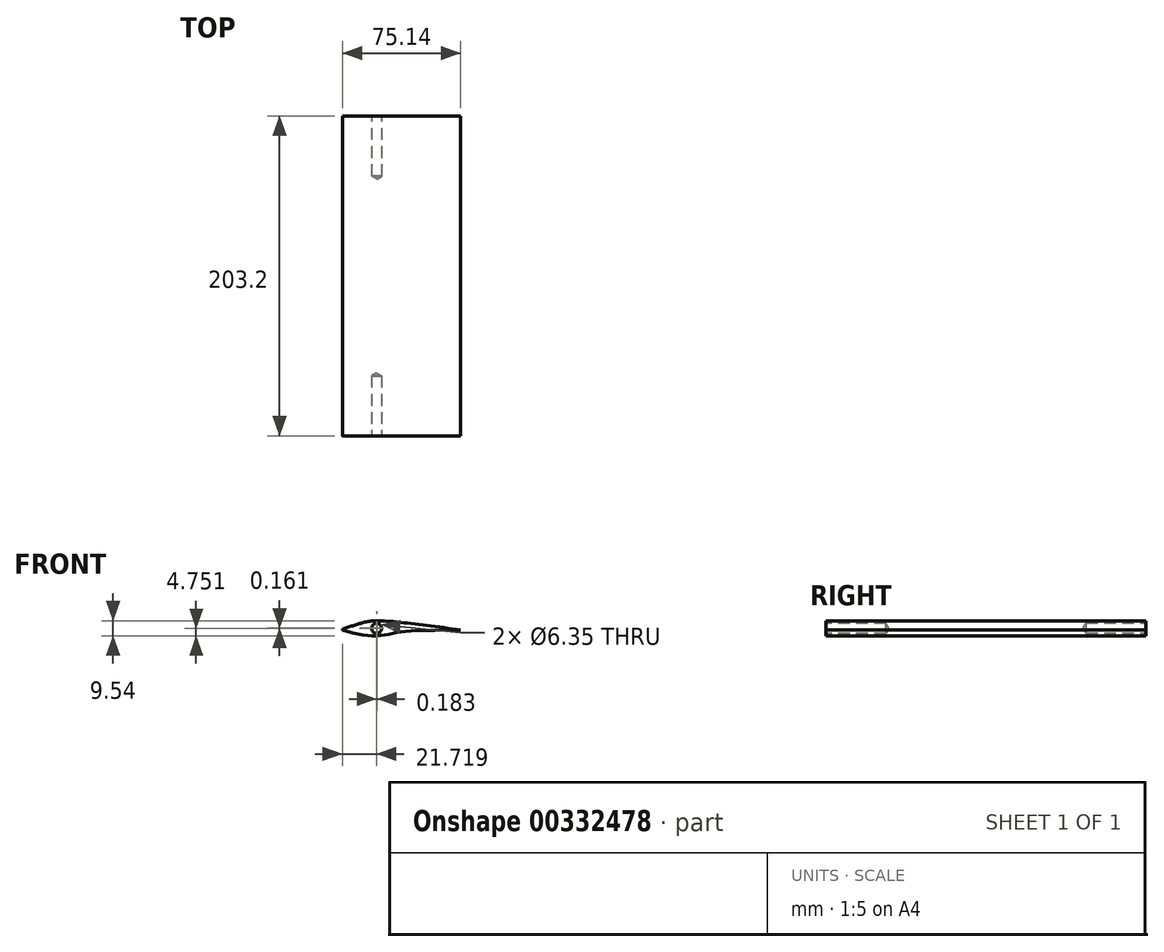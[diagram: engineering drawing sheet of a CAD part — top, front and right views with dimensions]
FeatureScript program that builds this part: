
annotation { "Feature Type Name" : "Feature", "Feature Type Description" : "" }
export const myFeature = defineFeature(function(context is Context, id is Id, definition is map)
    precondition{}
    {
        {
            var Q0;
            Q0=qCreatedBy(makeId("Front.planeOp"),FACE);
            var sketch = newSketch(context, id + "F0", { "sketchPlane" : qUnion([Q0])});
            skLineSegment(sketch, "E0", {"start": v(-15.24, -3.9) * mm, "end": v(-15.24, -3.9) * mm});
            skFitSpline(sketch, "E1", {"points": [v(-38.1, 0) * mm, v(-27.43, 3.47) * mm, v(-15.5, 5.63) * mm, v(38.1, 0) * mm], "startDerivative": vector(46.4, 16.4) * mm, "endDerivative": vector(122.48, -13.67) * mm});
            skFitSpline(sketch, "E2", {"points": [v(-38.1, 0) * mm, v(-15.24, -3.9) * mm, v(1.87, -1.13) * mm, v(38.1, 0) * mm], "startDerivative": vector(68.69, -19.73) * mm, "endDerivative": vector(99.76, 4.28) * mm});
            skPoint(sketch, "E3.endSnap0", {"position": v(-15.24, 3.44) * mm});
            skPoint(sketch, "E4.orphan", {"position": v(0, 0) * mm});
            skArc(sketch, "E5.trimOffspring", {"start": v(-15.2, 5.63) * mm, "mid": v(-15.22, 5.63) * mm, "end": v(-15.24, 5.63) * mm});
            skPoint(sketch, "E6.end.orphan", {"position": v(-15.22, 6.02) * mm});
            skPoint(sketch, "E7.trimOffspring.end.orphan", {"position": v(-15.24, -7.6) * mm});
            skSolve(sketch);
        }
        {
            var Q0;
            Q0 = qSketchRegion(id + "F0", true);
            extrude(context, id + "F1", {"entities" : qUnion([Q0]), "oppositeDirection" : true, "depth" : 203.2 * mm});
        }
        {
            var Q0;
            {var subQ0=sQuery(id+"F0.wireOp",EDGE,"E2");var subQ1=sQuery(id+"F0.wireOp",EDGE,"E1");Q0=makeQuery(id+"F1.opExtrude","SWEPT_EDGE",EDGE,{"disambiguationData":[OSD([subQ1,subQ0]),TDD([makeQuery(id+"F0.imprint","INTERSECT",VERTEX,{"disambiguationData":[OD(0.0)],"derivedFrom":[subQ1,subQ0]})])]});}
            fillet(context, id + "F2", {"entities" : qUnion([Q0]), "radius" : 0.46 * mm, "tangentPropagation" : true, "allowEdgeOverflow" : false});
        }
        {
            var Q0;
            Q0=makeQuery(id+"F1.opExtrude","CAP_FACE",FACE,{"disambiguationData":[OSD([sQuery(id+"F0.wireOp",EDGE,"E1"),sQuery(id+"F0.wireOp",EDGE,"E2")])],"isStart":false});
            var sketch = newSketch(context, id + "F3", { "sketchPlane" : qUnion([Q0])});
            skPoint(sketch, "E8", {"position": v(15.14, 1.01) * mm});
            skSolve(sketch);
        }
        {
            var Q0;
            Q0=sQuery(id+"F3.wireOp",VERTEX,"E8");
            var Q1;
            Q1=makeQuery(id+"F1.opExtrude","SWEPT_BODY",BODY,{"disambiguationData":[OSD([sQuery(id+"F0.wireOp",EDGE,"E1"),sQuery(id+"F0.wireOp",EDGE,"E2")])]});
            hole(context, id + "F4", {"style" : HoleStyle.SIMPLE, "endStyle" : HoleEndStyle.BLIND, "holeDiameter" : 6.35 * mm, "holeDepth" : 38.1 * mm, "tappedDepth" : 12.7 * mm, "tapClearance" : 3, "locations" : qUnion([Q0]), "scope" : qUnion([Q1])});
        }
        {
            var Q0;
            Q0=qCreatedBy(makeId("Front.planeOp"),FACE);
            var sketch = newSketch(context, id + "F5", { "sketchPlane" : qUnion([Q0])});
            skPoint(sketch, "E9", {"position": v(-15.32, 0.85) * mm});
            skSolve(sketch);
        }
        {
            var Q0;
            Q0=sQuery(id+"F5.wireOp",VERTEX,"E9");
            var Q1;
            Q1=makeQuery(id+"F1.opExtrude","SWEPT_BODY",BODY,{"disambiguationData":[OSD([sQuery(id+"F0.wireOp",EDGE,"E1"),sQuery(id+"F0.wireOp",EDGE,"E2")])]});
            hole(context, id + "F6", {"style" : HoleStyle.SIMPLE, "endStyle" : HoleEndStyle.BLIND, "holeDiameter" : 6.35 * mm, "holeDepth" : 38.1 * mm, "tappedDepth" : 12.7 * mm, "tapClearance" : 3, "locations" : qUnion([Q0]), "scope" : qUnion([Q1])});
        }
    });
